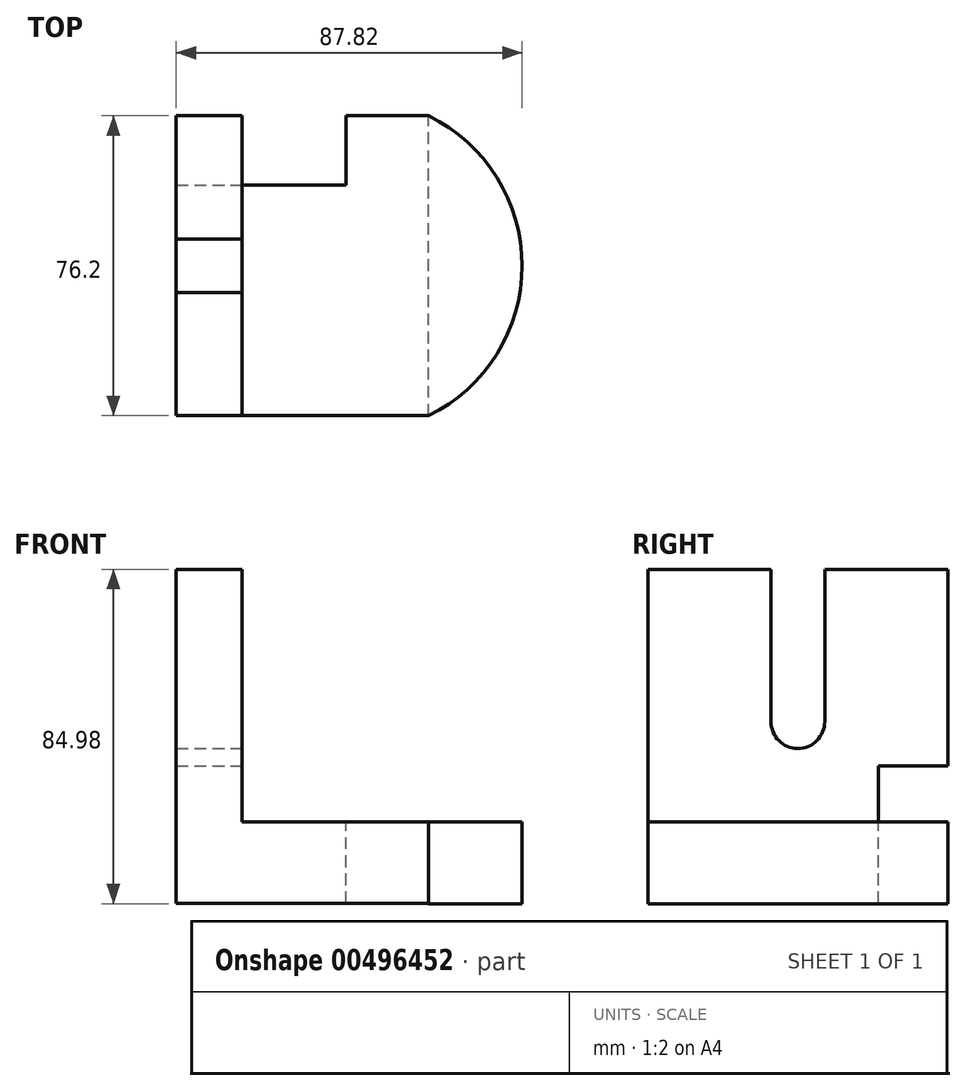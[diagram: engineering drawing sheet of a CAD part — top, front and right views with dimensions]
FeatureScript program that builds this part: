
annotation { "Feature Type Name" : "Feature", "Feature Type Description" : "" }
export const myFeature = defineFeature(function(context is Context, id is Id, definition is map)
    precondition{}
    {
        {
            var Q0;
            Q0=qCreatedBy(makeId("Front.planeOp"),FACE);
            var sketch = newSketch(context, id + "F0", { "sketchPlane" : qUnion([Q0])});
            skLineSegment(sketch, "E0", {"start": v(-16.68, 38.72) * mm, "end": v(-16.68, -46.18) * mm});
            skLineSegment(sketch, "E1", {"start": v(-16.68, -46.18) * mm, "end": v(47.44, -46.18) * mm});
            skLineSegment(sketch, "E2", {"start": v(47.44, -46.18) * mm, "end": v(47.44, -25.44) * mm});
            skLineSegment(sketch, "E3", {"start": v(47.44, -25.44) * mm, "end": v(0, -25.44) * mm});
            skLineSegment(sketch, "E4", {"start": v(0, -25.44) * mm, "end": v(0, 38.72) * mm});
            skLineSegment(sketch, "E5", {"start": v(0, 38.72) * mm, "end": v(-16.68, 38.72) * mm});
            skSolve(sketch);
        }
        {
            var Q0;
            Q0 = qSketchRegion(id + "F0", true);
            extrude(context, id + "F1", {"entities" : qUnion([Q0]), "endBound" : BoundingType.SYMMETRIC, "depth" : 76.2 * mm});
        }
        {
            var Q0;
            Q0=makeQuery(id+"F1.opExtrude","SWEPT_FACE",FACE,{"disambiguationData":[OSD([sQuery(id+"F0.wireOp",EDGE,"E3")])]});
            var sketch = newSketch(context, id + "F2", { "sketchPlane" : qUnion([Q0])});
            skArc(sketch, "E6", {"start": v(47.44, -38.1) * mm, "mid": v(71.14, 0) * mm, "end": v(47.44, 38.1) * mm});
            skSolve(sketch);
        }
        {
            var Q0;
            Q0 = qSketchRegion(id + "F2", true);
            var Q1;
            Q1=makeQuery(id+"F2.imprint","IMPRINT",FACE,{"disambiguationData":[TD([[makeQuery(id+"F2.imprint","IMPRINT",EDGE,{"derivedFrom":sQuery(id+"F2.wireOp",EDGE,"E6")}),1.0]])]});
            extrude(context, id + "F3", {"entities" : qUnion([Q0, Q1]), "operationType" : NewBodyOperationType.ADD, "oppositeDirection" : true, "depth" : 20.83 * mm});
        }
        {
            var Q0;
            Q0=makeQuery(id+"F1.opExtrude","SWEPT_FACE",FACE,{"disambiguationData":[OSD([sQuery(id+"F0.wireOp",EDGE,"E4")])]});
            var sketch = newSketch(context, id + "F4", { "sketchPlane" : qUnion([Q0])});
            skLineSegment(sketch, "E7.bottom", {"start": v(6.82, 0) * mm, "end": v(-6.82, 0) * mm});
            skLineSegment(sketch, "E7.top", {"start": v(6.82, 41.13) * mm, "end": v(-6.82, 41.13) * mm});
            skLineSegment(sketch, "E7.left", {"start": v(6.82, 0) * mm, "end": v(6.82, 41.13) * mm});
            skLineSegment(sketch, "E7.right", {"start": v(-6.82, 0) * mm, "end": v(-6.82, 41.13) * mm});
            skPoint(sketch, "E7.middle", {"position": v(0, 20.56) * mm});
            skCircle(sketch, "E8", {"center": v(0, 0) * mm, "radius": 6.82 * mm});
            skSolve(sketch);
        }
        {
            var Q0;
            {var subQ0=sQuery(id+"F4.wireOp",EDGE,"E8");var subQ1=sQuery(id+"F4.wireOp",EDGE,"E7.left");var subQ2=sQuery(id+"F4.wireOp",EDGE,"E7.bottom");var subQ3=makeQuery(id+"F4.imprint","INTERSECT",VERTEX,{"derivedFrom":[subQ2,subQ1,subQ0]});Q0=makeQuery(id+"F4.imprint","IMPRINT",FACE,{"disambiguationData":[TD([[makeQuery(id+"F4.imprint","IMPRINT",EDGE,{"disambiguationData":[TD([[subQ3,-1.0]])],"derivedFrom":subQ1}),1.0]])]});}
            var Q1;
            {var subQ0=sQuery(id+"F4.wireOp",EDGE,"E7.top");Q1=makeQuery(id+"F4.imprint","IMPRINT",FACE,{"disambiguationData":[TD([[makeQuery(id+"F4.imprint","IMPRINT",EDGE,{"derivedFrom":subQ0}),1.0]])]});}
            var Q2;
            {var subQ0=sQuery(id+"F4.wireOp",EDGE,"E7.bottom");Q2=makeQuery(id+"F4.imprint","IMPRINT",FACE,{"disambiguationData":[TD([[makeQuery(id+"F4.imprint","IMPRINT",EDGE,{"derivedFrom":subQ0}),-1.0]])]});}
            var Q3;
            {var subQ0=sQuery(id+"F4.wireOp",EDGE,"E7.bottom");Q3=makeQuery(id+"F4.imprint","IMPRINT",FACE,{"disambiguationData":[TD([[makeQuery(id+"F4.imprint","IMPRINT",EDGE,{"derivedFrom":subQ0}),1.0]])]});}
            extrude(context, id + "F5", {"entities" : qUnion([Q0, Q1, Q2, Q3]), "operationType" : NewBodyOperationType.REMOVE, "oppositeDirection" : true, "depth" : 50.8 * mm});
        }
        {
            var Q0;
            {var subQ0=sQuery(id+"F0.wireOp",EDGE,"E3");Q0=makeQuery(id+"F3.boolean.opBoolean","MERGE",FACE,{"derivedFrom":[makeQuery(id+"F1.opExtrude","SWEPT_FACE",FACE,{"disambiguationData":[OSD([subQ0])]}),makeQuery(id+"F3.opExtrude","CAP_FACE",FACE,{"disambiguationData":[OSD([sQuery(id+"F0.wireOp",EDGE,"E2"),subQ0,sQuery(id+"F2.wireOp",EDGE,"E6")])],"isStart":true})]});}
            var sketch = newSketch(context, id + "F6", { "sketchPlane" : qUnion([Q0])});
            skLineSegment(sketch, "E9", {"start": v(0, 20.5) * mm, "end": v(26.4, 20.5) * mm});
            skLineSegment(sketch, "E10", {"start": v(26.4, 20.5) * mm, "end": v(26.4, 38.1) * mm});
            skSolve(sketch);
        }
        {
            var Q0;
            {var subQ0=sQuery(id+"F6.wireOp",EDGE,"E9");Q0=makeQuery(id+"F6.imprint","IMPRINT",FACE,{"disambiguationData":[TD([[makeQuery(id+"F6.imprint","IMPRINT",EDGE,{"derivedFrom":subQ0}),1.0]])]});}
            extrude(context, id + "F7", {"entities" : qUnion([Q0]), "operationType" : NewBodyOperationType.REMOVE, "oppositeDirection" : true, "depth" : 50.8 * mm});
        }
        {
            var Q0;
            {var subQ0=sQuery(id+"F0.wireOp",EDGE,"E4");Q0=makeQuery(id+"F7.boolean.opBoolean","MERGE",FACE,{"derivedFrom":[makeQuery(id+"F1.opExtrude","SWEPT_FACE",FACE,{"disambiguationData":[OSD([subQ0])]}),makeQuery(id+"F7.opExtrude","SWEPT_FACE",FACE,{"disambiguationData":[OSD([sQuery(id+"F0.wireOp",EDGE,"E3"),subQ0])]})]});}
            var sketch = newSketch(context, id + "F8", { "sketchPlane" : qUnion([Q0])});
            skLineSegment(sketch, "E11", {"start": v(20.5, -25.44) * mm, "end": v(20.5, -11.3) * mm});
            skLineSegment(sketch, "E12", {"start": v(20.5, -11.3) * mm, "end": v(38.1, -11.3) * mm});
            skLineSegment(sketch, "E13", {"start": v(38.1, -11.3) * mm, "end": v(38.1, -46.18) * mm});
            skLineSegment(sketch, "E14", {"start": v(38.1, -46.18) * mm, "end": v(20.5, -46.18) * mm});
            skLineSegment(sketch, "E15", {"start": v(20.5, -46.18) * mm, "end": v(20.5, -25.44) * mm});
            skSolve(sketch);
        }
        {
            var Q0;
            Q0=makeQuery(id+"F8.imprint","IMPRINT",FACE,{"disambiguationData":[TD([[makeQuery(id+"F8.imprint","IMPRINT",EDGE,{"derivedFrom":sQuery(id+"F8.wireOp",EDGE,"E11")}),-1.0]])]});
            extrude(context, id + "F9", {"entities" : qUnion([Q0]), "operationType" : NewBodyOperationType.REMOVE, "oppositeDirection" : true, "depth" : 50.8 * mm});
        }
    });
